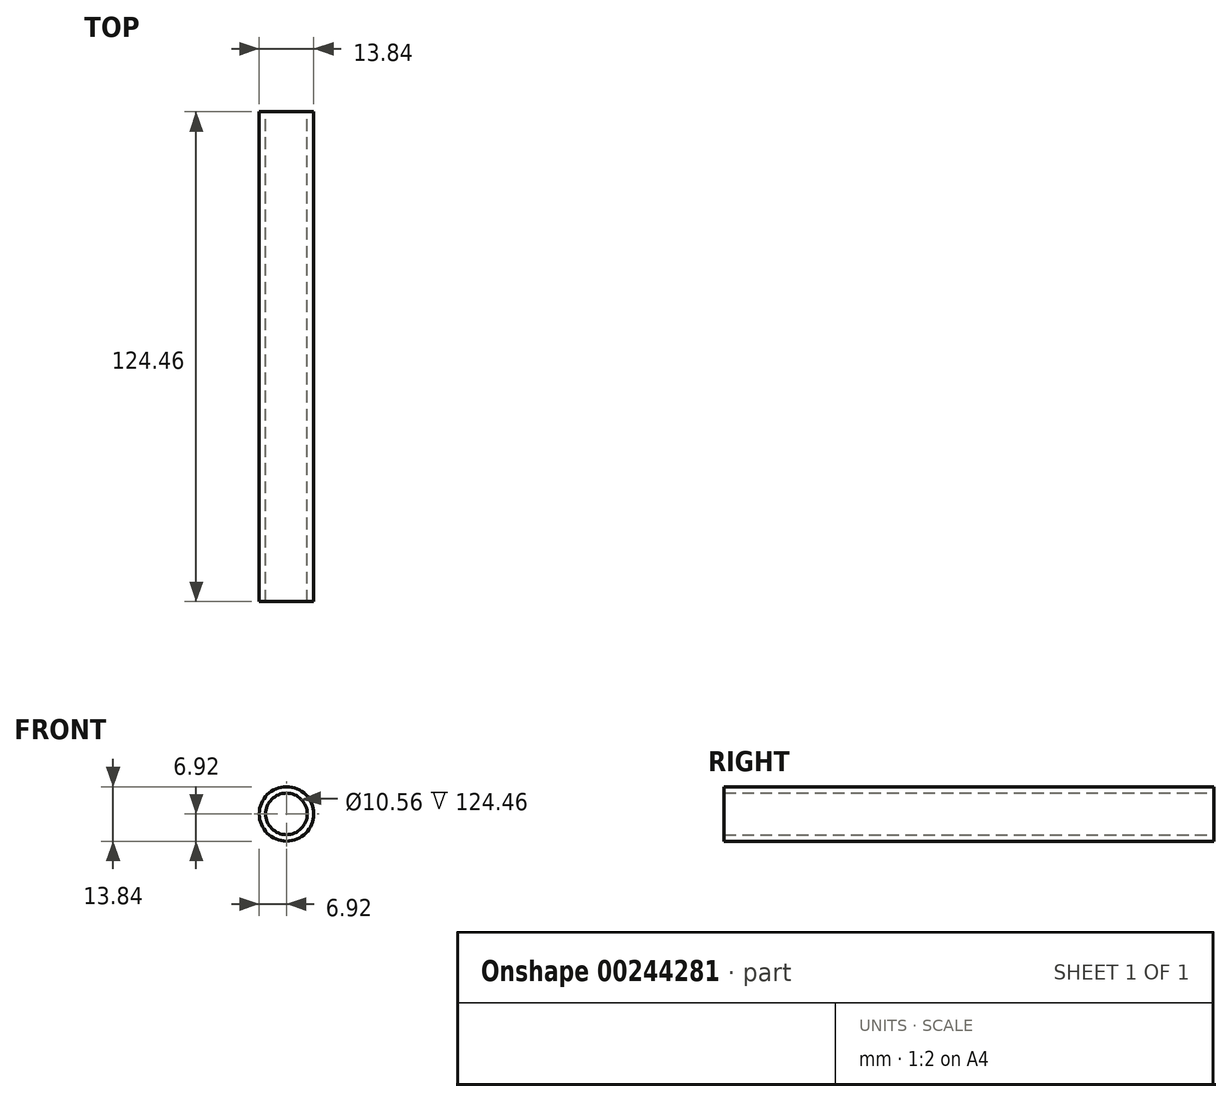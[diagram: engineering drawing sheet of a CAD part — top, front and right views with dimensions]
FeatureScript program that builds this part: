
annotation { "Feature Type Name" : "Feature", "Feature Type Description" : "" }
export const myFeature = defineFeature(function(context is Context, id is Id, definition is map)
    precondition{}
    {
        {
            var Q0;
            Q0=qCreatedBy(makeId("Front.planeOp"),FACE);
            var sketch = newSketch(context, id + "F0", { "sketchPlane" : qUnion([Q0])});
            skCircle(sketch, "E0", {"center": v(0, 0) * mm, "radius": 6.92 * mm});
            skCircle(sketch, "E1", {"center": v(0, 0) * mm, "radius": 5.28 * mm});
            skSolve(sketch);
        }
        {
            var Q0;
            Q0 = qSketchRegion(id + "F0", true);
            extrude(context, id + "F1", {"entities" : qUnion([Q0]), "depth" : 62.23 * mm, "hasSecondDirection" : true, "secondDirectionOppositeDirection" : true, "secondDirectionDepth" : 62.23 * mm});
        }
        {
            var Q0;
            Q0=qCreatedBy(makeId("Right.planeOp"),FACE);
            var sketch = newSketch(context, id + "F2", { "sketchPlane" : qUnion([Q0])});
            skArc(sketch, "E2", {"start": v(62.14, 0) * mm, "mid": v(0, 61.94) * mm, "end": v(-62.14, 0) * mm});
            skSolve(sketch);
        }
        {
            var Q0;
            Q0=sQuery(id+"F2.wireOp",EDGE,"E2");
            var Q1;
            Q1=makeQuery(id+"F1.opExtrude","SWEPT_FACE",FACE,{"disambiguationData":[OSD([sQuery(id+"F0.wireOp",EDGE,"E0")])]});
            revolve(context, id + "F3", {"bodyType" : ToolBodyType.SURFACE, "surfaceEntities" : qUnion([Q0]), "axis" : qUnion([Q1]), "revolveType" : RevolveType.FULL});
        }
        {
            var Q0;
            Q0 = qSketchRegion(id + "F0", true);
            extrude(context, id + "F4", {"entities" : qUnion([Q0]), "operationType" : NewBodyOperationType.ADD, "depth" : 25.4 * mm});
        }
    });
